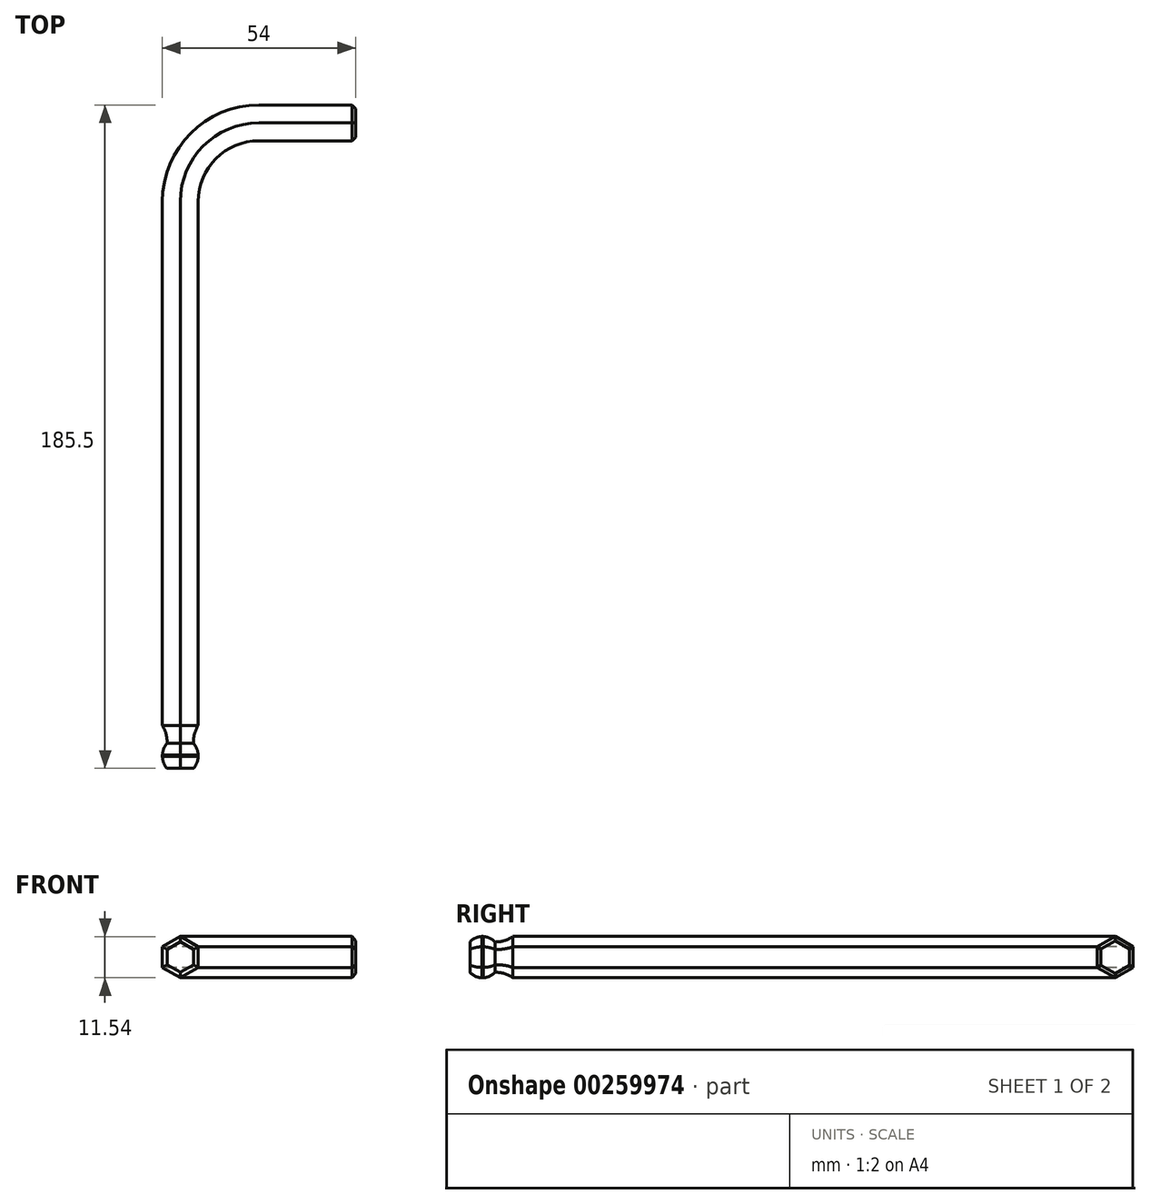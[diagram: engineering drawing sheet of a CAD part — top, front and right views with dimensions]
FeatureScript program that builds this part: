
annotation { "Feature Type Name" : "Feature", "Feature Type Description" : "" }
export const myFeature = defineFeature(function(context is Context, id is Id, definition is map)
    precondition{}
    {
        {
            var Q0;
            Q0=qCreatedBy(makeId("Top.planeOp"),FACE);
            var sketch = newSketch(context, id + "F0", { "sketchPlane" : qUnion([Q0]), "disableImprinting" : false});
            skLineSegment(sketch, "E0", {"start": v(0, 0) * mm, "end": v(0, 158.5) * mm});
            skArc(sketch, "E1", {"start": v(22, 180.5) * mm, "mid": v(6.44, 174.06) * mm, "end": v(0, 158.5) * mm});
            skLineSegment(sketch, "E2", {"start": v(22, 180.5) * mm, "end": v(49, 180.5) * mm});
            skSolve(sketch);
        }
        {
            var Q0;
            Q0=qCreatedBy(makeId("Right.planeOp"),FACE);
            cPlane(context, id + "F1", {"entities" : qUnion([Q0]), "cplaneType" : CPlaneType.OFFSET, "offset" : 49 * mm, "width" : 150 * mm, "height" : 150 * mm});
        }
        {
            var Q0;
            Q0=qCreatedBy(id+"F1.planeOp",FACE);
            var sketch = newSketch(context, id + "F2", { "sketchPlane" : qUnion([Q0])});
            skCircle(sketch, "E3.cCircle", {"center": v(180.5, 0) * mm, "radius": 5 * mm, "construction": true});
            skLineSegment(sketch, "E3.0", {"start": v(175.5, -2.89) * mm, "end": v(175.5, 2.89) * mm});
            skLineSegment(sketch, "E3.1", {"start": v(175.5, 2.89) * mm, "end": v(180.5, 5.77) * mm});
            skLineSegment(sketch, "E3.2", {"start": v(180.5, 5.77) * mm, "end": v(185.5, 2.89) * mm});
            skLineSegment(sketch, "E3.3", {"start": v(185.5, 2.89) * mm, "end": v(185.5, -2.89) * mm});
            skLineSegment(sketch, "E3.4", {"start": v(185.5, -2.89) * mm, "end": v(180.5, -5.77) * mm});
            skLineSegment(sketch, "E3.5", {"start": v(180.5, -5.77) * mm, "end": v(175.5, -2.89) * mm});
            skPoint(sketch, "E3.0.midPoint", {"position": v(175.5, 0) * mm});
            skSolve(sketch);
        }
        {
            var Q0;
            Q0=makeQuery(id+"F2.imprint","IMPRINT",FACE,{"disambiguationData":[TD([[makeQuery(id+"F2.imprint","IMPRINT",EDGE,{"derivedFrom":sQuery(id+"F2.wireOp",EDGE,"E3.0")}),-1.0]])]});
            var Q1;
            Q1 = qConstructionFilter(qBodyType(qCreatedBy(id + "F0" ,EDGE), BodyType.WIRE), ConstructionObject.NO);
            sweep(context, id + "F3", {"profiles" : qUnion([Q0]), "path" : qUnion([Q1])});
        }
        {
            var Q0;
            Q0=makeQuery(id+"F3.opSweep","CAP_FACE",FACE,{"disambiguationData":[OSD([sQuery(id+"F0.wireOp",VERTEX,"E2.end"),sQuery(id+"F2.wireOp",EDGE,"E3.0"),sQuery(id+"F2.wireOp",EDGE,"E3.1"),sQuery(id+"F2.wireOp",EDGE,"E3.2"),sQuery(id+"F2.wireOp",EDGE,"E3.3"),sQuery(id+"F2.wireOp",EDGE,"E3.4"),sQuery(id+"F2.wireOp",EDGE,"E3.5")])],"isStart":true});
            chamfer(context, id + "F4", {"entities" : qUnion([Q0]), "width" : 1 * mm, "tangentPropagation" : true});
        }
        {
            var Q0;
            Q0=qCreatedBy(makeId("Right.planeOp"),FACE);
            var sketch = newSketch(context, id + "F5", { "sketchPlane" : qUnion([Q0])});
            skArc(sketch, "E4", {"start": v(12, -5.77) * mm, "mid": v(9.63, -4.6) * mm, "end": v(7, -4.25) * mm});
            skArc(sketch, "E5", {"start": v(0, -4.25) * mm, "mid": v(3.5, -5.78) * mm, "end": v(7, -4.25) * mm});
            skLineSegment(sketch, "E6", {"start": v(12, -5.77) * mm, "end": v(12, -7.25) * mm});
            skLineSegment(sketch, "E7", {"start": v(12, -7.25) * mm, "end": v(0, -7.25) * mm});
            skLineSegment(sketch, "E8", {"start": v(0, -7.25) * mm, "end": v(0, -4.25) * mm});
            skSolve(sketch);
        }
        {
            var Q0;
            Q0 = qSketchRegion(id + "F5", true);
            var Q1;
            Q1=makeQuery(id+"F3.opSweep","CAP_EDGE",EDGE,{"disambiguationData":[OSD([sQuery(id+"F0.wireOp",VERTEX,"E0.start"),sQuery(id+"F2.wireOp",EDGE,"E3.4")])],"isStart":false});
            var Q2;
            Q2=makeQuery(id+"F3.opSweep","CAP_EDGE",EDGE,{"disambiguationData":[OSD([sQuery(id+"F0.wireOp",VERTEX,"E0.start"),sQuery(id+"F2.wireOp",EDGE,"E3.3")])],"isStart":false});
            var Q3;
            Q3=makeQuery(id+"F3.opSweep","CAP_EDGE",EDGE,{"disambiguationData":[OSD([sQuery(id+"F0.wireOp",VERTEX,"E0.start"),sQuery(id+"F2.wireOp",EDGE,"E3.2")])],"isStart":false});
            var Q4;
            Q4=makeQuery(id+"F3.opSweep","CAP_EDGE",EDGE,{"disambiguationData":[OSD([sQuery(id+"F0.wireOp",VERTEX,"E0.start"),sQuery(id+"F2.wireOp",EDGE,"E3.1")])],"isStart":false});
            var Q5;
            Q5=makeQuery(id+"F3.opSweep","CAP_EDGE",EDGE,{"disambiguationData":[OSD([sQuery(id+"F0.wireOp",VERTEX,"E0.start"),sQuery(id+"F2.wireOp",EDGE,"E3.0")])],"isStart":false});
            var Q6;
            Q6=makeQuery(id+"F3.opSweep","CAP_EDGE",EDGE,{"disambiguationData":[OSD([sQuery(id+"F0.wireOp",VERTEX,"E0.start"),sQuery(id+"F2.wireOp",EDGE,"E3.5")])],"isStart":false});
            sweep(context, id + "F6", {"operationType" : NewBodyOperationType.REMOVE, "profiles" : qUnion([Q0]), "path" : qUnion([Q1, Q2, Q3, Q4, Q5, Q6])});
        }
    });
